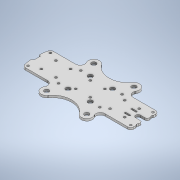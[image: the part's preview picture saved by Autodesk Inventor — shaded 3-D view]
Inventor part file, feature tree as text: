
AUTODESK INVENTOR PART (.ipt)
format: ipt  version: 2020 (Build 240168000, 168)  size: 360,448 bytes
history: native  units: mm
features: extrude x2, sketch x2
ambient origin geometry x8: Origin, YZ Plane, XZ Plane, XY Plane, X Axis, Y Axis, Z Axis, Center Point
bodies: Solid1 (feature_tree)
feature tree (4):
  extrude  "fill my holes daddy"  Depth=3.0mm
  extrude  "3m holes in the frunk"  Depth=3.1mm
  sketch  "Sketch1"  dims[d0=3.0mm d1=0.0mm d2=3.1mm]
  sketch  "Sketch2"  dims[d3=3.1mm d4=3.1mm d5=3.1mm d6=0.0mm d7=0.0mm]
